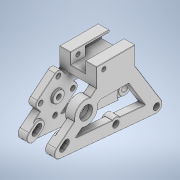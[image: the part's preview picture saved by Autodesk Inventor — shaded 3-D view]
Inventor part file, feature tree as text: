
AUTODESK INVENTOR PART (.ipt)
format: ipt  version: 2021 (Build 250183000, 183)  size: 1,183,744 bytes
history: native  units: mm
features: extrude x16, sketch x13, plane x2, mirror x2, fillet x2, projected_geometry x1
ambient origin geometry x8: Origin, YZ Plane, XZ Plane, XY Plane, X Axis, Y Axis, Z Axis, Center Point
bodies: Solid1 (feature_tree)
feature tree (36):
  extrude  "Extrusion1"  Depth=8.0mm
  sketch  "Sketch2"  dims[d0=8.0mm d1=8.0mm]
  extrude  "Extrusion2"  Depth=5.0mm
  extrude  "Extrusion3"  Depth=8.0mm
  extrude  "Extrusion4"  Depth=16.0mm
  plane  "Work Plane2"
  extrude  "Extrusion23"  Depth=16.0mm
  mirror  "Mirror2"
  extrude  "Extrusion24"  Depth=36.0mm
  extrude  "Extrusion25"  Depth=52.5mm
  extrude  "Extrusion26"  Depth=55.0mm
  sketch  "Sketch21"  dims[d17=40.0mm d20=52.5mm]
  extrude  "Extrusion27"  Depth=10.0mm TaperAngle=0.0deg
  extrude  "Extrusion28"  Depth=3.0mm TaperAngle=0.0deg
  extrude  "Extrusion29"  Depth=0.25mm TaperAngle=0.0deg
  extrude  "Extrusion30"  Depth=16.0mm
  extrude  "Extrusion31"  Depth=0.5mm
  extrude  "Extrusion37"  Depth=0.5mm
  extrude  "Extrusion36"  Depth=0.5mm
  plane  "Work Plane3"
  extrude  "Extrusion39"  Depth=0.5mm
  mirror  "Mirror4"
  fillet  "Fillet10"  Radius=10.0mm
  fillet  "Fillet11"  Radius=8.0mm
  sketch  "Sketch3"  dims[d3=75.0mm d4=5.0mm]
  sketch  "Sketch4"  dims[d7=8.0mm d8=55.0mm]
  projected_geometry  "Projected Loop1"
  sketch  "Sketch18"  dims[d9=7.0mm d12=16.0mm]
  sketch  "Sketch19"  dims[d13=16.0mm d14=16.0mm]
  sketch  "Sketch20"  dims[d15=22.0mm d16=36.0mm]
  sketch  "Sketch22"  dims[d21=26.25mm d22=55.0mm]
  sketch  "Sketch23"  dims[d26=10.0mm d27=0.0mm d28=2.75mm d29=0.0mm]
  sketch  "Sketch24"  dims[d30=26.0mm d31=3.0mm d32=0.0mm]
  sketch  "Sketch29"  dims[d34=16.0mm d35=0.25mm d36=0.0mm]
  sketch  "Sketch30"  dims[d37=12.25mm d55=16.0mm]
  sketch  "Sketch32"  dims[d56=0.5mm d57=0.5mm d58=45.0mm d61=6.0mm d62=36.0mm d63=10.0mm d64=8.0mm d164=50.0mm d165=0.0mm d166=50.0mm d167=0.0mm d168=25.0mm d169=0.0mm d170=32.0mm d171=12.75mm d172=0.0mm d173=22.0mm d174=7.0mm d175=0.0mm d176=17.0mm d177=0.0mm d178=0.0mm d179=15.5mm d180=15.5mm d181=3.0mm d182=6.0mm d183=13.0mm d184=40.0mm d186=360.0deg d188=10.0mm d189=0.0mm d190=10.0mm d191=0.0mm d192=3.0mm d193=0.0mm d194=22.0mm d195=2.0mm d196=0.0mm d204=0.0mm d205=0.0mm d233=15.0mm d234=2.5mm d235=12.5mm d236=5.0mm d237=15.0mm d238=2.5mm d239=12.5mm d240=5.0mm d241=0.5mm d242=0.5mm d246=5.0mm d247=10.0mm d248=7.5mm d249=0.0mm d250=0.0mm d261=40.0mm d262=2.5mm d263=20.0mm d264=15.0mm d265=0.0mm d266=0.5mm d267=0.5mm d293=4.0mm d294=8.0mm d296=5.6mm d297=8.0mm d298=6.375mm d299=10.0mm d300=0.0mm d223=0.5mm d224=0.872665mm d225=0.5mm d226=0.872665mm]
